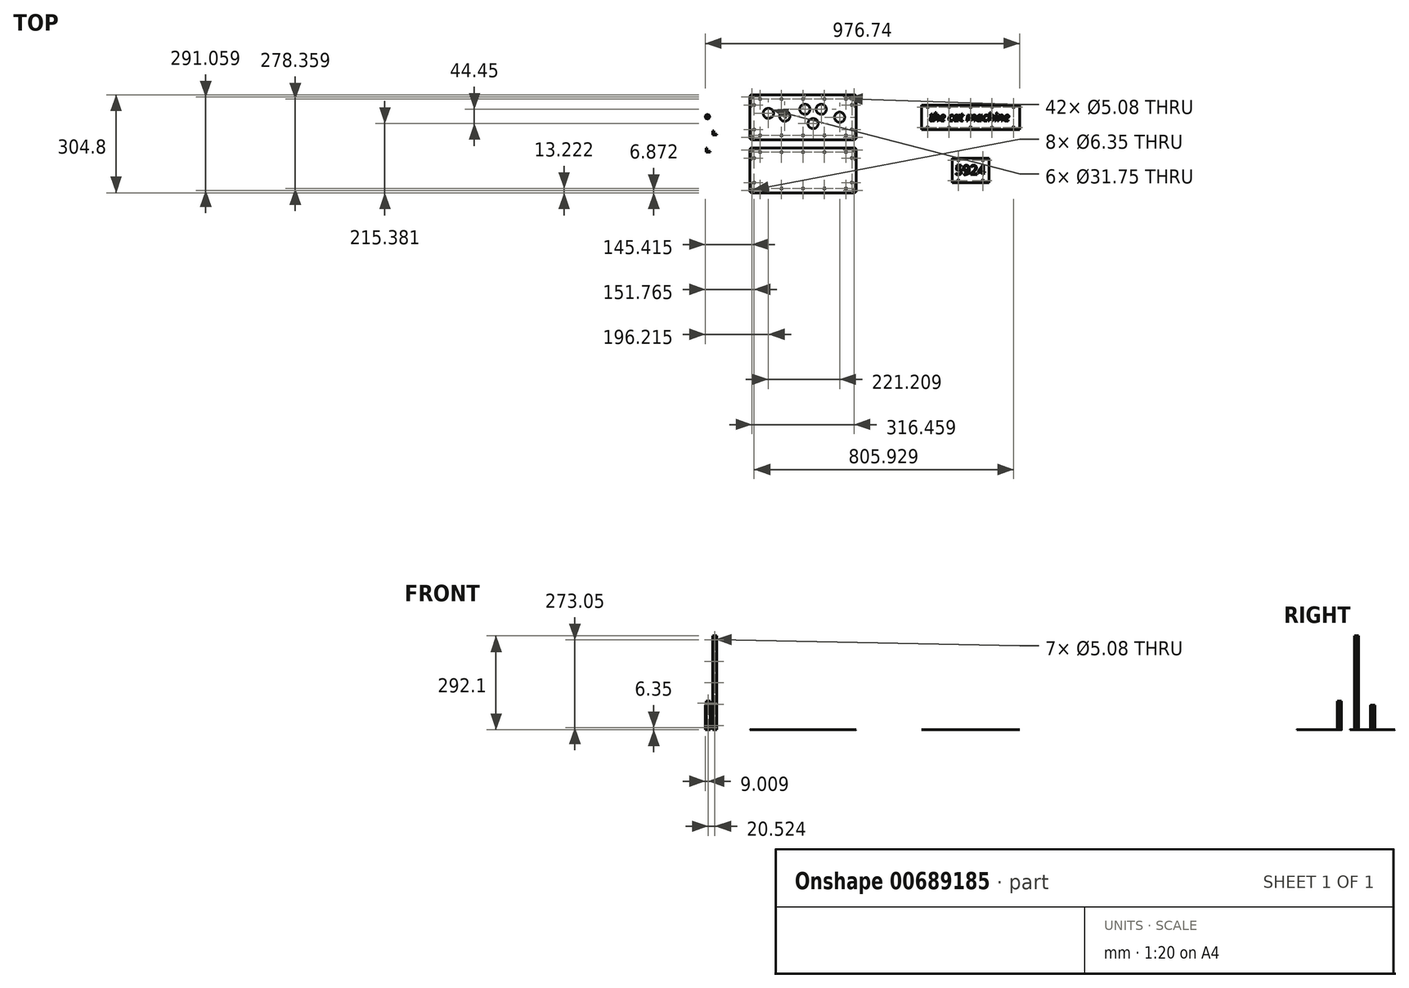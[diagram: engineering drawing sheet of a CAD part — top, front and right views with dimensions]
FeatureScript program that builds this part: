
annotation { "Feature Type Name" : "Feature", "Feature Type Description" : "" }
export const myFeature = defineFeature(function(context is Context, id is Id, definition is map)
    precondition{}
    {
        {
            assignVariable(context, id + "F0", {"name" : "standoff_height", "anyValue" : 76.2 * mm});
        }
        {
            var Q0;
            Q0=qCreatedBy(makeId("Top.planeOp"),FACE);
            var sketch = newSketch(context, id + "F1", { "sketchPlane" : qUnion([Q0])});
            skLineSegment(sketch, "E0.bottom", {"start": v(-132.13, 122.08) * mm, "end": v(198.07, 122.08) * mm});
            skLineSegment(sketch, "E0.top", {"start": v(-132.13, -17.62) * mm, "end": v(198.07, -17.62) * mm});
            skLineSegment(sketch, "E0.left", {"start": v(-132.13, 122.08) * mm, "end": v(-132.13, -17.62) * mm});
            skLineSegment(sketch, "E0.right", {"start": v(198.07, 122.08) * mm, "end": v(198.07, -17.62) * mm});
            skPoint(sketch, "E0.middle", {"position": v(32.97, 52.23) * mm});
            skCircle(sketch, "E1", {"center": v(-74.46, 64.41) * mm, "radius": 15.88 * mm});
            skCircle(sketch, "E2", {"center": v(-23.66, 55.45) * mm, "radius": 15.88 * mm});
            skLineSegment(sketch, "E3.bottom", {"start": v(-125.26, 115.21) * mm, "end": v(191.2, 115.21) * mm, "construction": true});
            skLineSegment(sketch, "E3.top", {"start": v(-125.26, -10.75) * mm, "end": v(191.2, -10.75) * mm, "construction": true});
            skLineSegment(sketch, "E3.left", {"start": v(-125.26, 115.21) * mm, "end": v(-125.26, -10.75) * mm, "construction": true});
            skLineSegment(sketch, "E3.right", {"start": v(191.2, 115.21) * mm, "end": v(191.2, -10.75) * mm, "construction": true});
            skCircle(sketch, "E4", {"center": v(-125.26, 115.21) * mm, "radius": 3.18 * mm});
            skCircle(sketch, "E5", {"center": v(191.2, 115.21) * mm, "radius": 3.18 * mm});
            skCircle(sketch, "E6", {"center": v(191.2, -10.75) * mm, "radius": 3.18 * mm});
            skCircle(sketch, "E7", {"center": v(-125.26, -10.75) * mm, "radius": 3.18 * mm});
            skLineSegment(sketch, "E8", {"start": v(-23.66, 55.45) * mm, "end": v(-74.46, 64.41) * mm, "construction": true});
            skLineSegment(sketch, "E9", {"start": v(-23.66, 55.45) * mm, "end": v(-23.66, 64.41) * mm, "construction": true});
            skLineSegment(sketch, "E10", {"start": v(-23.66, 64.41) * mm, "end": v(-74.46, 64.41) * mm, "construction": true});
            skCircle(sketch, "E11", {"center": v(38.8, 77.11) * mm, "radius": 15.88 * mm});
            skCircle(sketch, "E12", {"center": v(89.6, 77.11) * mm, "radius": 15.88 * mm});
            skCircle(sketch, "E13", {"center": v(64.2, 32.66) * mm, "radius": 15.88 * mm});
            skLineSegment(sketch, "E14", {"start": v(38.8, 77.11) * mm, "end": v(64.2, 32.66) * mm, "construction": true});
            skLineSegment(sketch, "E15", {"start": v(89.6, 77.11) * mm, "end": v(64.2, 32.66) * mm, "construction": true});
            skLineSegment(sketch, "E16", {"start": v(38.8, 77.11) * mm, "end": v(89.6, 77.11) * mm, "construction": true});
            skCircle(sketch, "E17", {"center": v(146.75, 52.23) * mm, "radius": 15.88 * mm});
            skLineSegment(sketch, "E18.bottom", {"start": v(-132.13, -43.02) * mm, "end": v(198.07, -43.02) * mm});
            skLineSegment(sketch, "E18.top", {"start": v(-132.13, -182.72) * mm, "end": v(198.07, -182.72) * mm});
            skLineSegment(sketch, "E18.left", {"start": v(-132.13, -43.02) * mm, "end": v(-132.13, -182.72) * mm});
            skLineSegment(sketch, "E18.right", {"start": v(198.07, -43.02) * mm, "end": v(198.07, -182.72) * mm});
            skPoint(sketch, "E18.middle", {"position": v(32.97, -112.87) * mm});
            skLineSegment(sketch, "E19.bottom", {"start": v(-125.26, -49.89) * mm, "end": v(191.2, -49.89) * mm, "construction": true});
            skLineSegment(sketch, "E19.top", {"start": v(-125.26, -175.85) * mm, "end": v(191.2, -175.85) * mm, "construction": true});
            skLineSegment(sketch, "E19.left", {"start": v(-125.26, -49.89) * mm, "end": v(-125.26, -175.85) * mm, "construction": true});
            skLineSegment(sketch, "E19.right", {"start": v(191.2, -49.89) * mm, "end": v(191.2, -175.85) * mm, "construction": true});
            skCircle(sketch, "E20", {"center": v(-125.26, -49.89) * mm, "radius": 3.18 * mm});
            skCircle(sketch, "E21", {"center": v(-125.26, -175.85) * mm, "radius": 3.18 * mm});
            skCircle(sketch, "E22", {"center": v(191.2, -175.85) * mm, "radius": 3.18 * mm});
            skCircle(sketch, "E23", {"center": v(191.2, -49.89) * mm, "radius": 3.18 * mm});
            skLineSegment(sketch, "E24", {"start": v(146.75, 115.21) * mm, "end": v(146.75, -10.75) * mm, "construction": true});
            skLineSegment(sketch, "E25", {"start": v(-100.38, -4.4) * mm, "end": v(-33.7, -4.4) * mm, "construction": true});
            skLineSegment(sketch, "E26", {"start": v(-33.7, -4.4) * mm, "end": v(32.97, -4.4) * mm, "construction": true});
            skLineSegment(sketch, "E27", {"start": v(32.97, -4.4) * mm, "end": v(99.65, -4.4) * mm, "construction": true});
            skLineSegment(sketch, "E28", {"start": v(99.65, -4.4) * mm, "end": v(166.32, -4.4) * mm, "construction": true});
            skCircle(sketch, "E29", {"center": v(-100.38, -4.4) * mm, "radius": 2.54 * mm});
            skCircle(sketch, "E30", {"center": v(-33.7, -4.4) * mm, "radius": 2.54 * mm});
            skCircle(sketch, "E31", {"center": v(32.97, -4.4) * mm, "radius": 2.54 * mm});
            skCircle(sketch, "E32", {"center": v(99.65, -4.4) * mm, "radius": 2.54 * mm});
            skCircle(sketch, "E33", {"center": v(166.32, -4.4) * mm, "radius": 2.54 * mm});
            skPoint(sketch, "E34", {"position": v(32.97, -17.62) * mm});
            skLineSegment(sketch, "E35", {"start": v(-118.9, 90.33) * mm, "end": v(-118.9, 52.23) * mm, "construction": true});
            skLineSegment(sketch, "E36", {"start": v(-118.9, 52.23) * mm, "end": v(-118.9, 14.13) * mm, "construction": true});
            skPoint(sketch, "E37", {"position": v(-125.26, 52.23) * mm});
            skCircle(sketch, "E38", {"center": v(-118.9, 14.13) * mm, "radius": 2.54 * mm});
            skCircle(sketch, "E39", {"center": v(-118.9, 52.23) * mm, "radius": 2.54 * mm, "construction": true});
            skCircle(sketch, "E40", {"center": v(-118.9, 90.33) * mm, "radius": 2.54 * mm});
            skLineSegment(sketch, "E41", {"start": v(299.67, 122.08) * mm, "end": v(299.67, -182.72) * mm, "construction": true});
            skLineSegment(sketch, "E42", {"start": v(198.07, 60.22) * mm, "end": v(299.67, 60.22) * mm, "construction": true});
            skLineSegment(sketch, "E43.bottom", {"start": v(401.27, 90.33) * mm, "end": v(706.07, 90.33) * mm});
            skLineSegment(sketch, "E43.top", {"start": v(401.27, 14.13) * mm, "end": v(706.07, 14.13) * mm});
            skLineSegment(sketch, "E43.left", {"start": v(401.27, 90.33) * mm, "end": v(401.27, 14.13) * mm});
            skLineSegment(sketch, "E43.right", {"start": v(706.07, 90.33) * mm, "end": v(706.07, 14.13) * mm});
            skPoint(sketch, "E43.middle", {"position": v(553.67, 52.23) * mm});
            skLineSegment(sketch, "E44", {"start": v(415.5, 52.23) * mm, "end": v(691.85, 52.23) * mm, "construction": true});
            skLineSegment(sketch, "E45", {"start": v(553.67, 78.87) * mm, "end": v(553.67, 25.59) * mm, "construction": true});
            skLineSegment(sketch, "E46", {"start": v(299.67, 45.07) * mm, "end": v(401.27, 45.07) * mm, "construction": true});
            skLineSegment(sketch, "E47", {"start": v(420.32, 20.48) * mm, "end": v(487, 20.48) * mm, "construction": true});
            skLineSegment(sketch, "E48", {"start": v(487, 20.48) * mm, "end": v(553.67, 20.48) * mm, "construction": true});
            skLineSegment(sketch, "E49", {"start": v(553.67, 20.48) * mm, "end": v(620.35, 20.48) * mm, "construction": true});
            skLineSegment(sketch, "E50", {"start": v(620.35, 20.48) * mm, "end": v(687.02, 20.48) * mm, "construction": true});
            skCircle(sketch, "E51", {"center": v(420.32, 20.48) * mm, "radius": 2.54 * mm});
            skCircle(sketch, "E52", {"center": v(487, 20.48) * mm, "radius": 2.54 * mm});
            skCircle(sketch, "E53", {"center": v(553.67, 20.48) * mm, "radius": 2.54 * mm});
            skCircle(sketch, "E54", {"center": v(620.35, 20.48) * mm, "radius": 2.54 * mm});
            skCircle(sketch, "E55", {"center": v(687.02, 20.48) * mm, "radius": 2.54 * mm});
            skPoint(sketch, "E56", {"position": v(553.67, 14.13) * mm});
            skCircle(sketch, "E57.MirrorC", {"center": v(620.35, 83.98) * mm, "radius": 2.54 * mm});
            skCircle(sketch, "E58.MirrorC", {"center": v(553.67, 83.98) * mm, "radius": 2.54 * mm});
            skLineSegment(sketch, "E59.MirrorCS", {"start": v(487, 83.98) * mm, "end": v(553.67, 83.98) * mm, "construction": true});
            skLineSegment(sketch, "E60.MirrorCS", {"start": v(553.67, 83.98) * mm, "end": v(620.35, 83.98) * mm, "construction": true});
            skCircle(sketch, "E61.MirrorC", {"center": v(487, 83.98) * mm, "radius": 2.54 * mm});
            skLineSegment(sketch, "E62.MirrorCS", {"start": v(620.35, 83.98) * mm, "end": v(687.02, 83.98) * mm, "construction": true});
            skLineSegment(sketch, "E63.MirrorCS", {"start": v(420.32, 83.98) * mm, "end": v(487, 83.98) * mm, "construction": true});
            skCircle(sketch, "E64.MirrorC", {"center": v(687.02, 83.98) * mm, "radius": 2.54 * mm});
            skCircle(sketch, "E65.MirrorC", {"center": v(420.32, 83.98) * mm, "radius": 2.54 * mm});
            skLineSegment(sketch, "E66", {"start": v(-1.85, 52.23) * mm, "end": v(67.8, 52.23) * mm, "construction": true});
            skCircle(sketch, "E67.MirrorC", {"center": v(166.32, 108.86) * mm, "radius": 2.54 * mm});
            skCircle(sketch, "E68.MirrorC", {"center": v(99.65, 108.86) * mm, "radius": 2.54 * mm});
            skCircle(sketch, "E69.MirrorC", {"center": v(32.97, 108.86) * mm, "radius": 2.54 * mm});
            skCircle(sketch, "E70.MirrorC", {"center": v(-33.7, 108.86) * mm, "radius": 2.54 * mm});
            skCircle(sketch, "E71.MirrorC", {"center": v(-100.38, 108.86) * mm, "radius": 2.54 * mm});
            skLineSegment(sketch, "E72", {"start": v(32.97, 73.53) * mm, "end": v(32.97, 30.93) * mm, "construction": true});
            skCircle(sketch, "E73.MirrorC", {"center": v(184.85, 52.23) * mm, "radius": 2.54 * mm, "construction": true});
            skCircle(sketch, "E74.MirrorC", {"center": v(184.85, 90.33) * mm, "radius": 2.54 * mm});
            skCircle(sketch, "E75.MirrorC", {"center": v(184.85, 14.13) * mm, "radius": 2.54 * mm});
            skLineSegment(sketch, "E76.MirrorCS", {"start": v(184.85, 52.23) * mm, "end": v(184.85, 14.13) * mm, "construction": true});
            skLineSegment(sketch, "E77.MirrorCS", {"start": v(184.85, 90.33) * mm, "end": v(184.85, 52.23) * mm, "construction": true});
            skLineSegment(sketch, "E78", {"start": v(-148.78, -30.32) * mm, "end": v(251.54, -30.32) * mm, "construction": true});
            skLineSegment(sketch, "E79", {"start": v(-92.96, -17.62) * mm, "end": v(-92.96, -43.02) * mm, "construction": true});
            skPoint(sketch, "E80", {"position": v(-92.96, -30.32) * mm});
            skCircle(sketch, "E81.MirrorC", {"center": v(-118.9, -74.77) * mm, "radius": 2.54 * mm});
            skCircle(sketch, "E82.MirrorC", {"center": v(-118.9, -150.97) * mm, "radius": 2.54 * mm});
            skCircle(sketch, "E83.MirrorC", {"center": v(-118.9, -112.87) * mm, "radius": 2.54 * mm, "construction": true});
            skLineSegment(sketch, "E84.MirrorCS", {"start": v(-118.9, -112.87) * mm, "end": v(-118.9, -74.77) * mm, "construction": true});
            skLineSegment(sketch, "E85.MirrorCS", {"start": v(-118.9, -150.97) * mm, "end": v(-118.9, -112.87) * mm, "construction": true});
            skLineSegment(sketch, "E86.MirrorCS", {"start": v(184.85, -112.87) * mm, "end": v(184.85, -74.77) * mm, "construction": true});
            skCircle(sketch, "E87.MirrorC", {"center": v(184.85, -150.97) * mm, "radius": 2.54 * mm});
            skCircle(sketch, "E88.MirrorC", {"center": v(184.85, -112.87) * mm, "radius": 2.54 * mm, "construction": true});
            skCircle(sketch, "E89.MirrorC", {"center": v(184.85, -74.77) * mm, "radius": 2.54 * mm});
            skLineSegment(sketch, "E90.MirrorCS", {"start": v(184.85, -150.97) * mm, "end": v(184.85, -112.87) * mm, "construction": true});
            skCircle(sketch, "E91.MirrorC", {"center": v(166.32, -169.5) * mm, "radius": 2.54 * mm});
            skCircle(sketch, "E92.MirrorC", {"center": v(99.65, -169.5) * mm, "radius": 2.54 * mm});
            skCircle(sketch, "E93.MirrorC", {"center": v(32.97, -169.5) * mm, "radius": 2.54 * mm});
            skCircle(sketch, "E94.MirrorC", {"center": v(-33.7, -169.5) * mm, "radius": 2.54 * mm});
            skCircle(sketch, "E95.MirrorC", {"center": v(-100.38, -169.5) * mm, "radius": 2.54 * mm});
            skCircle(sketch, "E96.MirrorC", {"center": v(99.65, -56.24) * mm, "radius": 2.54 * mm});
            skCircle(sketch, "E97.MirrorC", {"center": v(32.97, -56.24) * mm, "radius": 2.54 * mm});
            skLineSegment(sketch, "E98.MirrorCS", {"start": v(32.97, -56.24) * mm, "end": v(99.65, -56.24) * mm, "construction": true});
            skCircle(sketch, "E99.MirrorC", {"center": v(166.32, -56.24) * mm, "radius": 2.54 * mm});
            skLineSegment(sketch, "E100.MirrorCS", {"start": v(-33.7, -56.24) * mm, "end": v(32.97, -56.24) * mm, "construction": true});
            skLineSegment(sketch, "E101.MirrorCS", {"start": v(-100.38, -56.24) * mm, "end": v(-33.7, -56.24) * mm, "construction": true});
            skLineSegment(sketch, "E102.MirrorCS", {"start": v(99.65, -56.24) * mm, "end": v(166.32, -56.24) * mm, "construction": true});
            skCircle(sketch, "E103.MirrorC", {"center": v(-33.7, -56.24) * mm, "radius": 2.54 * mm});
            skCircle(sketch, "E104.MirrorC", {"center": v(-100.38, -56.24) * mm, "radius": 2.54 * mm});
            skLineSegment(sketch, "E105.bottom", {"start": v(496.52, -74.77) * mm, "end": v(610.82, -74.77) * mm});
            skLineSegment(sketch, "E105.top", {"start": v(496.52, -150.97) * mm, "end": v(610.82, -150.97) * mm});
            skLineSegment(sketch, "E105.left", {"start": v(496.52, -74.77) * mm, "end": v(496.52, -150.97) * mm});
            skLineSegment(sketch, "E105.right", {"start": v(610.82, -74.77) * mm, "end": v(610.82, -150.97) * mm});
            skPoint(sketch, "E105.middle", {"position": v(553.67, -112.87) * mm});
            skLineSegment(sketch, "E106", {"start": v(515.57, -81.12) * mm, "end": v(591.77, -81.12) * mm, "construction": true});
            skLineSegment(sketch, "E107", {"start": v(338.28, -112.87) * mm, "end": v(769.07, -112.87) * mm, "construction": true});
            skLineSegment(sketch, "E108", {"start": v(515.57, -144.62) * mm, "end": v(591.77, -144.62) * mm, "construction": true});
            skPoint(sketch, "E109", {"position": v(553.67, -81.12) * mm});
            skPoint(sketch, "E110", {"position": v(553.67, -144.62) * mm});
            skCircle(sketch, "E111", {"center": v(515.57, -144.62) * mm, "radius": 2.54 * mm});
            skCircle(sketch, "E112", {"center": v(591.77, -144.62) * mm, "radius": 2.54 * mm});
            skCircle(sketch, "E113", {"center": v(591.77, -81.12) * mm, "radius": 2.54 * mm});
            skCircle(sketch, "E114", {"center": v(515.57, -81.12) * mm, "radius": 2.54 * mm});
            skLineSegment(sketch, "E115", {"start": v(553.67, -81.12) * mm, "end": v(553.67, -144.62) * mm, "construction": true});
            skLineSegment(sketch, "E116", {"start": v(-100.38, -4.4) * mm, "end": v(-119.43, -4.4) * mm, "construction": true});
            skLineSegment(sketch, "E117", {"start": v(166.32, -4.4) * mm, "end": v(185.37, -4.4) * mm, "construction": true});
            skSolve(sketch);
        }
        {
            var Q0;
            Q0=makeQuery(id+"F1.imprint","IMPRINT",FACE,{"disambiguationData":[TD([[makeQuery(id+"F1.imprint","IMPRINT",EDGE,{"derivedFrom":sQuery(id+"F1.wireOp",EDGE,"E0.bottom")}),-1.0]])]});
            extrude(context, id + "F2", {"entities" : qUnion([Q0]), "depth" : 1 / 203.2 * mm, "offsetDistance" : 25.4 * mm});
        }
        {
            var Q0;
            Q0=makeQuery(id+"F1.imprint","IMPRINT",FACE,{"disambiguationData":[TD([[makeQuery(id+"F1.imprint","IMPRINT",EDGE,{"derivedFrom":sQuery(id+"F1.wireOp",EDGE,"E18.bottom")}),-1.0]])]});
            extrude(context, id + "F3", {"entities" : qUnion([Q0]), "depth" : 1 / 203.2 * mm, "offsetDistance" : 25.4 * mm});
        }
        {
            var Q0;
            Q0=makeQuery(id+"F1.imprint","IMPRINT",FACE,{"disambiguationData":[TD([[makeQuery(id+"F1.imprint","IMPRINT",EDGE,{"derivedFrom":sQuery(id+"F1.wireOp",EDGE,"E43.bottom")}),-1.0]])]});
            extrude(context, id + "F4", {"entities" : qUnion([Q0]), "depth" : 1 / 203.2 * mm, "offsetDistance" : 25.4 * mm});
        }
        {
            var Q0;
            Q0=makeQuery(id+"F2.opExtrude","SWEPT_EDGE",EDGE,{"disambiguationData":[OSD([sQuery(id+"F1.wireOp",EDGE,"E0.top"),sQuery(id+"F1.wireOp",EDGE,"E0.left")])]});
            var Q1;
            Q1=makeQuery(id+"F2.opExtrude","SWEPT_EDGE",EDGE,{"disambiguationData":[OSD([sQuery(id+"F1.wireOp",EDGE,"E0.bottom"),sQuery(id+"F1.wireOp",EDGE,"E0.left")])]});
            var Q2;
            Q2=makeQuery(id+"F2.opExtrude","SWEPT_EDGE",EDGE,{"disambiguationData":[OSD([sQuery(id+"F1.wireOp",EDGE,"E0.bottom"),sQuery(id+"F1.wireOp",EDGE,"E0.right")])]});
            var Q3;
            Q3=makeQuery(id+"F2.opExtrude","SWEPT_EDGE",EDGE,{"disambiguationData":[OSD([sQuery(id+"F1.wireOp",EDGE,"E0.top"),sQuery(id+"F1.wireOp",EDGE,"E0.right")])]});
            var Q4;
            Q4=makeQuery(id+"F3.opExtrude","SWEPT_EDGE",EDGE,{"disambiguationData":[OSD([sQuery(id+"F1.wireOp",EDGE,"E18.bottom"),sQuery(id+"F1.wireOp",EDGE,"E18.left")])]});
            var Q5;
            Q5=makeQuery(id+"F3.opExtrude","SWEPT_EDGE",EDGE,{"disambiguationData":[OSD([sQuery(id+"F1.wireOp",EDGE,"E18.top"),sQuery(id+"F1.wireOp",EDGE,"E18.left")])]});
            var Q6;
            Q6=makeQuery(id+"F3.opExtrude","SWEPT_EDGE",EDGE,{"disambiguationData":[OSD([sQuery(id+"F1.wireOp",EDGE,"E18.top"),sQuery(id+"F1.wireOp",EDGE,"E18.right")])]});
            var Q7;
            Q7=makeQuery(id+"F3.opExtrude","SWEPT_EDGE",EDGE,{"disambiguationData":[OSD([sQuery(id+"F1.wireOp",EDGE,"E18.bottom"),sQuery(id+"F1.wireOp",EDGE,"E18.right")])]});
            fillet(context, id + "F5", {"entities" : qUnion([Q0, Q1, Q2, Q3, Q4, Q5, Q6, Q7]), "radius" : 6.35 * mm, "tangentPropagation" : true, "allowEdgeOverflow" : false});
        }
        {
            var Q0;
            Q0=qCreatedBy(makeId("Top.planeOp"),FACE);
            var sketch = newSketch(context, id + "F6", { "sketchPlane" : qUnion([Q0])});
            skCircle(sketch, "E118", {"center": v(-263.92, 53.63) * mm, "radius": 2.55 * mm});
            skCircle(sketch, "E119.cCircle", {"center": v(-263.92, 53.63) * mm, "radius": 6.35 * mm, "construction": true});
            skLineSegment(sketch, "E119.0", {"start": v(-257.75, 50.62) * mm, "end": v(-261.67, 47.14) * mm});
            skLineSegment(sketch, "E119.1", {"start": v(-263.44, 46.78) * mm, "end": v(-268.42, 48.43) * mm});
            skLineSegment(sketch, "E119.2", {"start": v(-269.62, 49.79) * mm, "end": v(-270.67, 54.93) * mm});
            skLineSegment(sketch, "E119.3", {"start": v(-270.1, 56.64) * mm, "end": v(-266.17, 60.12) * mm});
            skLineSegment(sketch, "E119.4", {"start": v(-264.4, 60.48) * mm, "end": v(-259.43, 58.82) * mm});
            skLineSegment(sketch, "E119.5", {"start": v(-258.23, 57.47) * mm, "end": v(-257.18, 52.33) * mm});
            skPoint(sketch, "E119.0.midPoint", {"position": v(-259.71, 48.88) * mm});
            skArc(sketch, "E120", {"start": v(-269.62, 49.79) * mm, "mid": v(-269.07, 49.07) * mm, "end": v(-268.42, 48.43) * mm});
            skArc(sketch, "E121.trimOffspring", {"start": v(-270.1, 56.64) * mm, "mid": v(-270.44, 55.8) * mm, "end": v(-270.67, 54.93) * mm});
            skArc(sketch, "E122.trimOffspring", {"start": v(-264.4, 60.48) * mm, "mid": v(-265.3, 60.36) * mm, "end": v(-266.17, 60.12) * mm});
            skArc(sketch, "E123.trimOffspring", {"start": v(-258.23, 57.47) * mm, "mid": v(-258.78, 58.19) * mm, "end": v(-259.43, 58.82) * mm});
            skArc(sketch, "E124.trimOffspring", {"start": v(-257.75, 50.62) * mm, "mid": v(-257.4, 51.46) * mm, "end": v(-257.18, 52.33) * mm});
            skArc(sketch, "E125.trimOffspring", {"start": v(-263.44, 46.78) * mm, "mid": v(-262.55, 46.9) * mm, "end": v(-261.67, 47.14) * mm});
            skPoint(sketch, "E126.orphan", {"position": v(-269.41, 48.76) * mm});
            skPoint(sketch, "E127.orphan", {"position": v(-262.45, 46.45) * mm});
            skPoint(sketch, "E128.orphan", {"position": v(-256.97, 51.31) * mm});
            skPoint(sketch, "E129.orphan", {"position": v(-258.44, 58.5) * mm});
            skPoint(sketch, "E130.orphan", {"position": v(-265.4, 60.81) * mm});
            skPoint(sketch, "E131.orphan", {"position": v(-270.88, 55.95) * mm});
            skSolve(sketch);
        }
        {
            var Q0;
            Q0=makeQuery(id+"F6.imprint","IMPRINT",FACE,{"disambiguationData":[TD([[makeQuery(id+"F6.imprint","IMPRINT",EDGE,{"derivedFrom":sQuery(id+"F6.wireOp",EDGE,"E118")}),-1.0]])]});
            extrude(context, id + "F7", {"entities" : qUnion([Q0]), "depth" : getVariable(context, 'standoff_height'), "offsetDistance" : 25.4 * mm});
        }
        {
            var Q0;
            Q0=qCreatedBy(makeId("Top.planeOp"),FACE);
            var sketch = newSketch(context, id + "F8", { "sketchPlane" : qUnion([Q0])});
            skLineSegment(sketch, "E132", {"start": v(-247.49, 9.68) * mm, "end": v(-247.49, -3.02) * mm});
            skLineSegment(sketch, "E133", {"start": v(-247.49, -3.02) * mm, "end": v(-234.79, -3.02) * mm});
            skLineSegment(sketch, "E134", {"start": v(-234.79, -3.02) * mm, "end": v(-234.79, 0.16) * mm});
            skLineSegment(sketch, "E135", {"start": v(-234.79, 0.16) * mm, "end": v(-244.31, 0.16) * mm});
            skLineSegment(sketch, "E136", {"start": v(-244.31, 0.16) * mm, "end": v(-244.31, 9.68) * mm});
            skLineSegment(sketch, "E137", {"start": v(-244.31, 9.68) * mm, "end": v(-247.49, 9.68) * mm});
            skLineSegment(sketch, "E138", {"start": v(-268.01, -43.54) * mm, "end": v(-268.01, -56.24) * mm});
            skLineSegment(sketch, "E139", {"start": v(-268.01, -56.24) * mm, "end": v(-255.31, -56.24) * mm});
            skLineSegment(sketch, "E140", {"start": v(-255.31, -56.24) * mm, "end": v(-255.31, -53.07) * mm});
            skLineSegment(sketch, "E141", {"start": v(-255.31, -53.07) * mm, "end": v(-264.84, -53.07) * mm});
            skLineSegment(sketch, "E142", {"start": v(-264.84, -53.07) * mm, "end": v(-264.84, -43.54) * mm});
            skLineSegment(sketch, "E143", {"start": v(-264.84, -43.54) * mm, "end": v(-268.01, -43.54) * mm});
            skSolve(sketch);
        }
        {
            var Q0;
            Q0=makeQuery(id+"F8.imprint","IMPRINT",FACE,{"disambiguationData":[TD([[makeQuery(id+"F8.imprint","IMPRINT",EDGE,{"derivedFrom":sQuery(id+"F8.wireOp",EDGE,"E132")}),1.0]])]});
            extrude(context, id + "F9", {"entities" : qUnion([Q0]), "depth" : 292.1 * mm, "offsetDistance" : 25.4 * mm});
        }
        {
            var Q0;
            Q0=makeQuery(id+"F9.opExtrude","SWEPT_FACE",FACE,{"disambiguationData":[OSD([sQuery(id+"F8.wireOp",EDGE,"E132")])]});
            var sketch = newSketch(context, id + "F10", { "sketchPlane" : qUnion([Q0])});
            skLineSegment(sketch, "E144.0.0", {"start": v(-9.68, 0) * mm, "end": v(3.02, 0) * mm, "construction": true});
            skLineSegment(sketch, "E144.0.1", {"start": v(3.02, 0) * mm, "end": v(3.02, 292.1) * mm, "construction": true});
            skLineSegment(sketch, "E144.0.2", {"start": v(3.02, 292.1) * mm, "end": v(-9.68, 292.1) * mm, "construction": true});
            skLineSegment(sketch, "E144.0.3", {"start": v(-9.68, 292.1) * mm, "end": v(-9.68, 0) * mm, "construction": true});
            skLineSegment(sketch, "E145", {"start": v(-3.33, 279.4) * mm, "end": v(-3.33, 212.73) * mm, "construction": true});
            skLineSegment(sketch, "E146", {"start": v(-3.33, 212.73) * mm, "end": v(-3.33, 146.05) * mm, "construction": true});
            skLineSegment(sketch, "E147", {"start": v(-3.33, 146.05) * mm, "end": v(-3.33, 79.38) * mm, "construction": true});
            skLineSegment(sketch, "E148", {"start": v(-3.33, 79.38) * mm, "end": v(-3.33, 12.7) * mm, "construction": true});
            skPoint(sketch, "E149", {"position": v(3.02, 146.05) * mm});
            skLineSegment(sketch, "E150", {"start": v(-3.33, 12.7) * mm, "end": v(-3.33, -6.35) * mm, "construction": true});
            skLineSegment(sketch, "E151", {"start": v(-3.33, 279.4) * mm, "end": v(-3.33, 298.45) * mm, "construction": true});
            skSolve(sketch);
        }
        {
            var Q0;
            Q0=makeQuery(id+"F9.opExtrude","SWEPT_FACE",FACE,{"disambiguationData":[OSD([sQuery(id+"F8.wireOp",EDGE,"E133")])]});
            var sketch = newSketch(context, id + "F11", { "sketchPlane" : qUnion([Q0])});
            skLineSegment(sketch, "E152.0.0", {"start": v(-247.49, 0) * mm, "end": v(-234.79, 0) * mm, "construction": true});
            skLineSegment(sketch, "E152.0.1", {"start": v(-234.79, 0) * mm, "end": v(-234.79, 292.1) * mm, "construction": true});
            skLineSegment(sketch, "E152.0.2", {"start": v(-234.79, 292.1) * mm, "end": v(-247.49, 292.1) * mm, "construction": true});
            skLineSegment(sketch, "E152.0.3", {"start": v(-247.49, 292.1) * mm, "end": v(-247.49, 0) * mm, "construction": true});
            skLineSegment(sketch, "E153", {"start": v(-241.14, 279.4) * mm, "end": v(-241.14, 212.73) * mm, "construction": true});
            skPoint(sketch, "E153.startSnap0", {"position": v(-241.14, 292.1) * mm});
            skLineSegment(sketch, "E154", {"start": v(-241.14, 212.73) * mm, "end": v(-241.14, 146.05) * mm, "construction": true});
            skLineSegment(sketch, "E155", {"start": v(-241.14, 146.05) * mm, "end": v(-241.14, 79.38) * mm, "construction": true});
            skLineSegment(sketch, "E156", {"start": v(-241.14, 79.38) * mm, "end": v(-241.14, 12.7) * mm, "construction": true});
            skCircle(sketch, "E157", {"center": v(-241.14, 12.7) * mm, "radius": 2.54 * mm});
            skCircle(sketch, "E158", {"center": v(-241.14, 79.38) * mm, "radius": 2.54 * mm});
            skCircle(sketch, "E159", {"center": v(-241.14, 146.05) * mm, "radius": 2.54 * mm});
            skCircle(sketch, "E160", {"center": v(-241.14, 212.73) * mm, "radius": 2.54 * mm});
            skCircle(sketch, "E161", {"center": v(-241.14, 279.4) * mm, "radius": 2.54 * mm});
            skPoint(sketch, "E162", {"position": v(-247.49, 146.05) * mm});
            skLineSegment(sketch, "E163", {"start": v(-241.14, 12.7) * mm, "end": v(-241.14, -6.35) * mm, "construction": true});
            skLineSegment(sketch, "E164", {"start": v(-241.14, 279.4) * mm, "end": v(-241.14, 298.45) * mm, "construction": true});
            skSolve(sketch);
        }
        {
            var Q0;
            Q0=makeQuery(id+"F8.imprint","IMPRINT",FACE,{"disambiguationData":[TD([[makeQuery(id+"F8.imprint","IMPRINT",EDGE,{"derivedFrom":sQuery(id+"F8.wireOp",EDGE,"E138")}),1.0]])]});
            extrude(context, id + "F12", {"entities" : qUnion([Q0]), "depth" : 88.9 * mm, "offsetDistance" : 25.4 * mm});
        }
        {
            var Q0;
            Q0=makeQuery(id+"F12.opExtrude","SWEPT_FACE",FACE,{"disambiguationData":[OSD([sQuery(id+"F8.wireOp",EDGE,"E138")])]});
            var sketch = newSketch(context, id + "F13", { "sketchPlane" : qUnion([Q0])});
            skLineSegment(sketch, "E165.0.0", {"start": v(43.54, 0) * mm, "end": v(56.24, 0) * mm, "construction": true});
            skLineSegment(sketch, "E165.0.1", {"start": v(56.24, 0) * mm, "end": v(56.24, 88.9) * mm, "construction": true});
            skLineSegment(sketch, "E165.0.2", {"start": v(56.24, 88.9) * mm, "end": v(43.54, 88.9) * mm, "construction": true});
            skLineSegment(sketch, "E165.0.3", {"start": v(43.54, 88.9) * mm, "end": v(43.54, 0) * mm, "construction": true});
            skLineSegment(sketch, "E166", {"start": v(49.9, 82.55) * mm, "end": v(49.9, 6.35) * mm, "construction": true});
            skPoint(sketch, "E166.startSnap0", {"position": v(49.9, 88.9) * mm});
            skPoint(sketch, "E167", {"position": v(49.9, 44.45) * mm});
            skPoint(sketch, "E168", {"position": v(56.24, 44.45) * mm});
            skSolve(sketch);
        }
        {
            var Q0;
            Q0=makeQuery(id+"F12.opExtrude","SWEPT_FACE",FACE,{"disambiguationData":[OSD([sQuery(id+"F8.wireOp",EDGE,"E139")])]});
            var sketch = newSketch(context, id + "F14", { "sketchPlane" : qUnion([Q0])});
            skLineSegment(sketch, "E169.0.0", {"start": v(-268.01, 0) * mm, "end": v(-255.31, 0) * mm, "construction": true});
            skLineSegment(sketch, "E169.0.1", {"start": v(-255.31, 0) * mm, "end": v(-255.31, 88.9) * mm, "construction": true});
            skLineSegment(sketch, "E169.0.2", {"start": v(-255.31, 88.9) * mm, "end": v(-268.01, 88.9) * mm, "construction": true});
            skLineSegment(sketch, "E169.0.3", {"start": v(-268.01, 88.9) * mm, "end": v(-268.01, 0) * mm, "construction": true});
            skLineSegment(sketch, "E170", {"start": v(-261.66, 82.55) * mm, "end": v(-261.66, 6.35) * mm, "construction": true});
            skPoint(sketch, "E170.startSnap0", {"position": v(-261.66, 88.9) * mm});
            skPoint(sketch, "E171", {"position": v(-261.66, 44.45) * mm});
            skSolve(sketch);
        }
        {
            var Q0;
            Q0=sQuery(id+"F10.wireOp",VERTEX,"E145.start");
            var Q1;
            Q1=sQuery(id+"F10.wireOp",VERTEX,"E145.end");
            var Q2;
            Q2=sQuery(id+"F10.wireOp",VERTEX,"E146.end");
            var Q3;
            Q3=sQuery(id+"F10.wireOp",VERTEX,"E147.end");
            var Q4;
            Q4=sQuery(id+"F10.wireOp",VERTEX,"E148.end");
            var Q5;
            Q5=sQuery(id+"F11.wireOp",VERTEX,"E153.start");
            var Q6;
            Q6=sQuery(id+"F11.wireOp",VERTEX,"E153.end");
            var Q7;
            Q7=sQuery(id+"F11.wireOp",VERTEX,"E154.end");
            var Q8;
            Q8=sQuery(id+"F11.wireOp",VERTEX,"E155.end");
            var Q9;
            Q9=sQuery(id+"F11.wireOp",VERTEX,"E156.end");
            var Q10;
            Q10=sQuery(id+"F13.wireOp",VERTEX,"E166.start");
            var Q11;
            Q11=sQuery(id+"F13.wireOp",VERTEX,"E166.end");
            var Q12;
            Q12=sQuery(id+"F14.wireOp",VERTEX,"E170.start");
            var Q13;
            Q13=sQuery(id+"F14.wireOp",VERTEX,"E170.end");
            var Q14;
            Q14=makeQuery(id+"F9.opExtrude","SWEPT_BODY",BODY,{"disambiguationData":[OSD([sQuery(id+"F8.wireOp",EDGE,"E132"),sQuery(id+"F8.wireOp",EDGE,"E133"),sQuery(id+"F8.wireOp",EDGE,"E134"),sQuery(id+"F8.wireOp",EDGE,"E135"),sQuery(id+"F8.wireOp",EDGE,"E136"),sQuery(id+"F8.wireOp",EDGE,"E137")])]});
            var Q15;
            Q15=makeQuery(id+"F12.opExtrude","SWEPT_BODY",BODY,{"disambiguationData":[OSD([sQuery(id+"F8.wireOp",EDGE,"E138"),sQuery(id+"F8.wireOp",EDGE,"E139"),sQuery(id+"F8.wireOp",EDGE,"E140"),sQuery(id+"F8.wireOp",EDGE,"E141"),sQuery(id+"F8.wireOp",EDGE,"E142"),sQuery(id+"F8.wireOp",EDGE,"E143")])]});
            hole(context, id + "F15", {"style" : HoleStyle.SIMPLE, "endStyle" : HoleEndStyle.BLIND, "holeDiameter" : 5.08 * mm, "majorDiameter" : 6.35 * mm, "holeDepth" : 12.7 * mm, "isTappedThrough" : true, "tappedDepth" : 12.7 * mm, "tapClearance" : 3, "locations" : qUnion([Q0, Q1, Q2, Q3, Q4, Q5, Q6, Q7, Q8, Q9, Q10, Q11, Q12, Q13]), "scope" : qUnion([Q14, Q15])});
        }
        {
            var Q0;
            Q0=makeQuery(id+"F1.imprint","IMPRINT",FACE,{"disambiguationData":[TD([[makeQuery(id+"F1.imprint","IMPRINT",EDGE,{"derivedFrom":sQuery(id+"F1.wireOp",EDGE,"E105.bottom")}),-1.0]])]});
            extrude(context, id + "F16", {"entities" : qUnion([Q0]), "depth" : 1 / 203.2 * mm, "offsetDistance" : 25.4 * mm});
        }
        {
            var Q0;
            Q0=makeQuery(id+"F4.opExtrude","CAP_FACE",FACE,{"disambiguationData":[OSD([sQuery(id+"F1.wireOp",EDGE,"E43.bottom"),sQuery(id+"F1.wireOp",EDGE,"E43.top"),sQuery(id+"F1.wireOp",EDGE,"E43.left"),sQuery(id+"F1.wireOp",EDGE,"E43.right"),sQuery(id+"F1.wireOp",EDGE,"E51"),sQuery(id+"F1.wireOp",EDGE,"E52"),sQuery(id+"F1.wireOp",EDGE,"E53"),sQuery(id+"F1.wireOp",EDGE,"E54"),sQuery(id+"F1.wireOp",EDGE,"E55"),sQuery(id+"F1.wireOp",EDGE,"E57.MirrorC"),sQuery(id+"F1.wireOp",EDGE,"E58.MirrorC"),sQuery(id+"F1.wireOp",EDGE,"E61.MirrorC"),sQuery(id+"F1.wireOp",EDGE,"E64.MirrorC"),sQuery(id+"F1.wireOp",EDGE,"E65.MirrorC")])],"isStart":false});
            var sketch = newSketch(context, id + "F17", { "sketchPlane" : qUnion([Q0])});
            skText(sketch, "E172", { "text": "the cat machine", "fontName": "OpenSans-Italic.ttf"});
            skText(sketch, "E173", { "text": "5924\n", "fontName": "OpenSans-Regular.ttf"});
            const initialGuessF17  = {"E172": [0.42555, 0.04016, 1, 0, 0.0254], "E173": [0.50543, -0.12632, 1, 0, 0.02944]};
            skSetInitialGuess(sketch, initialGuessF17);
            skSolve(sketch);
        }
        {
            var Q0;
            Q0 = qSketchRegion(id + "F17", true);
            extrude(context, id + "F18", {"entities" : qUnion([Q0]), "operationType" : NewBodyOperationType.REMOVE, "oppositeDirection" : true, "depth" : 1 / 406.4 * mm, "offsetDistance" : 25.4 * mm});
        }
    });
